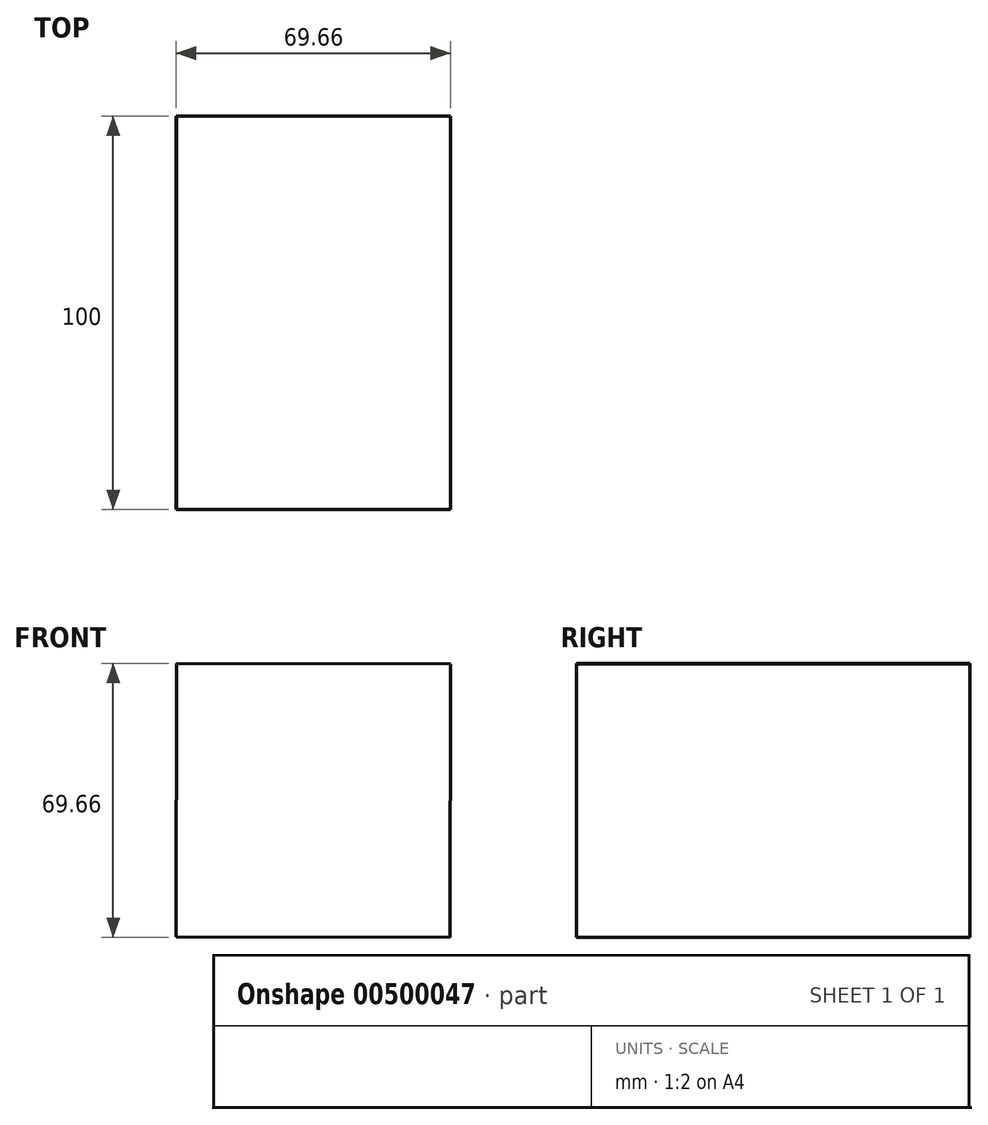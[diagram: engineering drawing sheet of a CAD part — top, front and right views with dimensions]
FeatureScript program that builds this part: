
annotation { "Feature Type Name" : "Feature", "Feature Type Description" : "" }
export const myFeature = defineFeature(function(context is Context, id is Id, definition is map)
    precondition{}
    {
        {
            var Q0;
            Q0=qCreatedBy(makeId("Front.planeOp"),FACE);
            var sketch = newSketch(context, id + "F0", { "sketchPlane" : qUnion([Q0])});
            skCircle(sketch, "E0.cCircle", {"center": v(0, 0) * mm, "radius": 49.16 * mm, "construction": true});
            skLineSegment(sketch, "E0.0", {"start": v(-34.69, 34.83) * mm, "end": v(34.83, 34.69) * mm});
            skLineSegment(sketch, "E0.1", {"start": v(34.83, 34.69) * mm, "end": v(34.69, -34.83) * mm});
            skLineSegment(sketch, "E0.2", {"start": v(34.69, -34.83) * mm, "end": v(-34.83, -34.69) * mm});
            skLineSegment(sketch, "E0.3", {"start": v(-34.83, -34.69) * mm, "end": v(-34.69, 34.83) * mm});
            skSolve(sketch);
        }
        {
            var Q0;
            Q0 = qSketchRegion(id + "F0", true);
            extrude(context, id + "F1", {"entities" : qUnion([Q0]), "depth" : 100 * mm});
        }
    });
